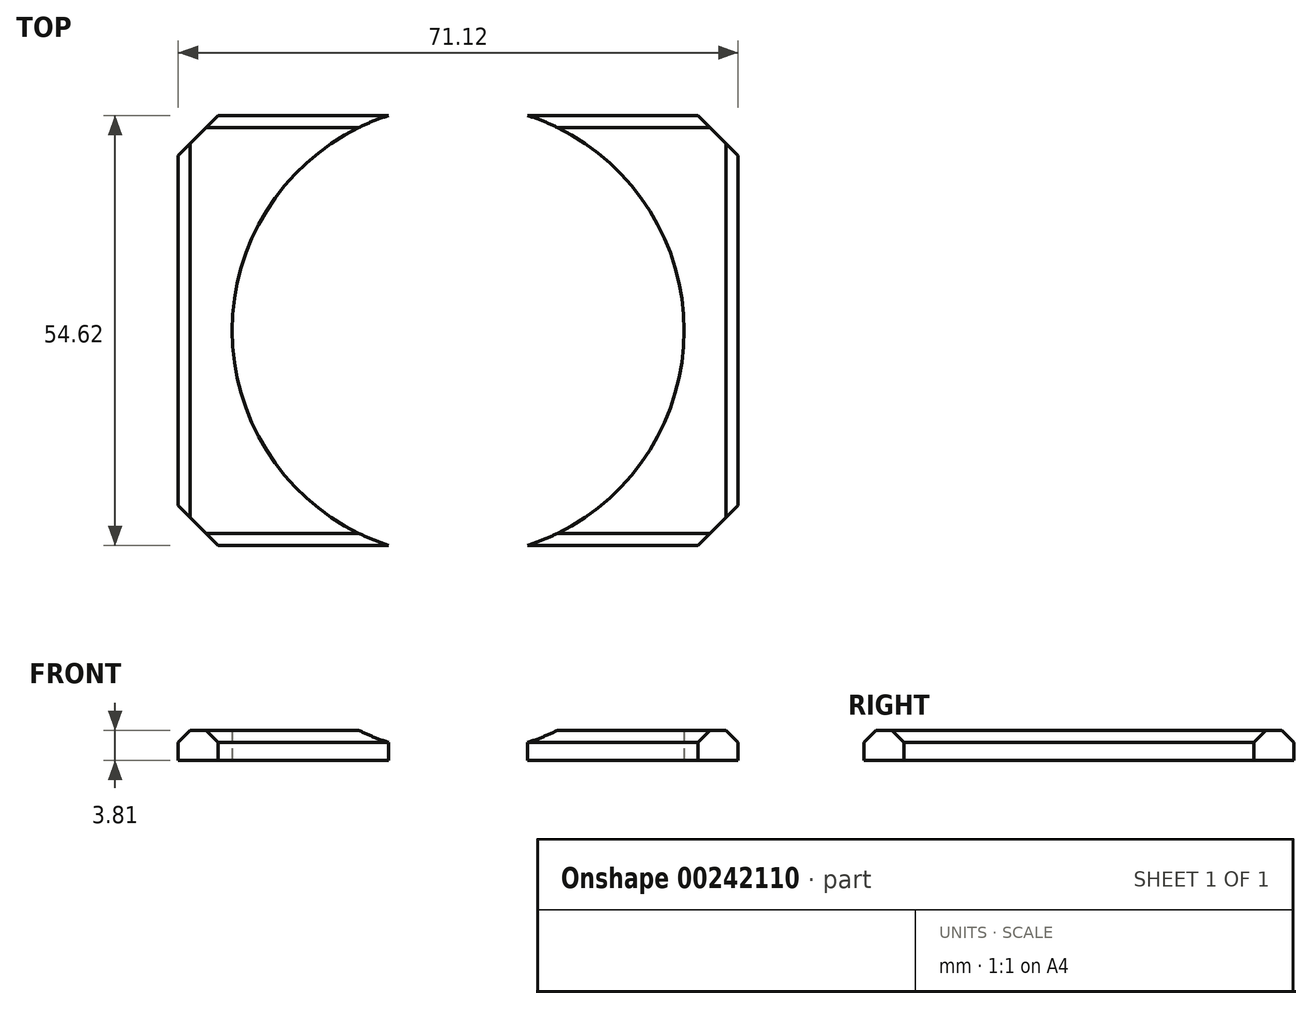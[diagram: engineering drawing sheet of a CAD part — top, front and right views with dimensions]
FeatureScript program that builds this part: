
annotation { "Feature Type Name" : "Feature", "Feature Type Description" : "" }
export const myFeature = defineFeature(function(context is Context, id is Id, definition is map)
    precondition{}
    {
        {
            var Q0;
            Q0=qCreatedBy(makeId("Top.planeOp"),FACE);
            var sketch = newSketch(context, id + "F0", { "sketchPlane" : qUnion([Q0])});
            skPoint(sketch, "E0.middle", {"position": v(0, 0) * mm});
            skLineSegment(sketch, "E1.0", {"start": v(-35.56, 27.3) * mm, "end": v(35.56, 27.3) * mm});
            skLineSegment(sketch, "E1.1", {"start": v(-35.56, 27.3) * mm, "end": v(-35.56, -27.3) * mm});
            skLineSegment(sketch, "E1.2", {"start": v(-35.56, -27.3) * mm, "end": v(35.56, -27.3) * mm});
            skLineSegment(sketch, "E1.3", {"start": v(35.56, 27.3) * mm, "end": v(35.56, -27.3) * mm});
            skCircle(sketch, "E2", {"center": v(0, 0) * mm, "radius": 28.7 * mm});
            skSolve(sketch);
        }
        {
            var Q0;
            {var subQ0=sQuery(id+"F0.wireOp",EDGE,"E1.1");Q0=makeQuery(id+"F0.imprint","IMPRINT",FACE,{"disambiguationData":[TD([[makeQuery(id+"F0.imprint","IMPRINT",EDGE,{"derivedFrom":subQ0}),1.0]])]});}
            var Q1;
            {var subQ0=sQuery(id+"F0.wireOp",EDGE,"E1.3");Q1=makeQuery(id+"F0.imprint","IMPRINT",FACE,{"disambiguationData":[TD([[makeQuery(id+"F0.imprint","IMPRINT",EDGE,{"derivedFrom":subQ0}),-1.0]])]});}
            extrude(context, id + "F1", {"entities" : qUnion([Q0, Q1]), "depth" : 3.8 * mm});
        }
        {
            var Q0;
            Q0=makeQuery(id+"F1.opExtrude","CAP_EDGE",EDGE,{"disambiguationData":[OSD([sQuery(id+"F0.wireOp",EDGE,"E1.1")])],"isStart":false});
            var Q1;
            {var subQ0=sQuery(id+"F0.wireOp",EDGE,"E1.0");Q1=makeQuery(id+"F1.opExtrude","CAP_EDGE",EDGE,{"disambiguationData":[OSD([subQ0]),TDD([makeQuery(id+"F0.imprint","IMPRINT",EDGE,{"disambiguationData":[TD([[makeQuery(id+"F0.imprint","INTERSECT",VERTEX,{"derivedFrom":[subQ0,sQuery(id+"F0.wireOp",EDGE,"E1.1")]}),-1.0]])],"derivedFrom":subQ0})])],"isStart":false});}
            var Q2;
            {var subQ0=sQuery(id+"F0.wireOp",EDGE,"E1.2");Q2=makeQuery(id+"F1.opExtrude","CAP_EDGE",EDGE,{"disambiguationData":[OSD([subQ0]),TDD([makeQuery(id+"F0.imprint","IMPRINT",EDGE,{"disambiguationData":[TD([[makeQuery(id+"F0.imprint","INTERSECT",VERTEX,{"derivedFrom":[sQuery(id+"F0.wireOp",EDGE,"E1.1"),subQ0]}),-1.0]])],"derivedFrom":subQ0})])],"isStart":false});}
            var Q3;
            {var subQ0=sQuery(id+"F0.wireOp",EDGE,"E1.2");Q3=makeQuery(id+"F1.opExtrude","CAP_EDGE",EDGE,{"disambiguationData":[OSD([subQ0]),TDD([makeQuery(id+"F0.imprint","IMPRINT",EDGE,{"disambiguationData":[TD([[makeQuery(id+"F0.imprint","INTERSECT",VERTEX,{"derivedFrom":[subQ0,sQuery(id+"F0.wireOp",EDGE,"E1.3")]}),1.0]])],"derivedFrom":subQ0})])],"isStart":false});}
            var Q4;
            Q4=makeQuery(id+"F1.opExtrude","CAP_EDGE",EDGE,{"disambiguationData":[OSD([sQuery(id+"F0.wireOp",EDGE,"E1.3")])],"isStart":false});
            var Q5;
            {var subQ0=sQuery(id+"F0.wireOp",EDGE,"E1.0");Q5=makeQuery(id+"F1.opExtrude","CAP_EDGE",EDGE,{"disambiguationData":[OSD([subQ0]),TDD([makeQuery(id+"F0.imprint","IMPRINT",EDGE,{"disambiguationData":[TD([[makeQuery(id+"F0.imprint","INTERSECT",VERTEX,{"derivedFrom":[subQ0,sQuery(id+"F0.wireOp",EDGE,"E1.3")]}),1.0]])],"derivedFrom":subQ0})])],"isStart":false});}
            chamfer(context, id + "F2", {"entities" : qUnion([Q0, Q1, Q2, Q3, Q4, Q5]), "width" : 1.52 * mm, "tangentPropagation" : true});
        }
        {
            var Q0;
            Q0=makeQuery(id+"F1.opExtrude","SWEPT_EDGE",EDGE,{"disambiguationData":[OSD([sQuery(id+"F0.wireOp",EDGE,"E1.2"),sQuery(id+"F0.wireOp",EDGE,"E1.3")])]});
            var Q1;
            Q1=makeQuery(id+"F1.opExtrude","SWEPT_EDGE",EDGE,{"disambiguationData":[OSD([sQuery(id+"F0.wireOp",EDGE,"E1.0"),sQuery(id+"F0.wireOp",EDGE,"E1.3")])]});
            var Q2;
            Q2=makeQuery(id+"F1.opExtrude","SWEPT_EDGE",EDGE,{"disambiguationData":[OSD([sQuery(id+"F0.wireOp",EDGE,"E1.1"),sQuery(id+"F0.wireOp",EDGE,"E1.2")])]});
            var Q3;
            Q3=makeQuery(id+"F1.opExtrude","SWEPT_EDGE",EDGE,{"disambiguationData":[OSD([sQuery(id+"F0.wireOp",EDGE,"E1.0"),sQuery(id+"F0.wireOp",EDGE,"E1.1")])]});
            chamfer(context, id + "F3", {"entities" : qUnion([Q0, Q1, Q2, Q3]), "width" : 5.08 * mm, "tangentPropagation" : true});
        }
    });
